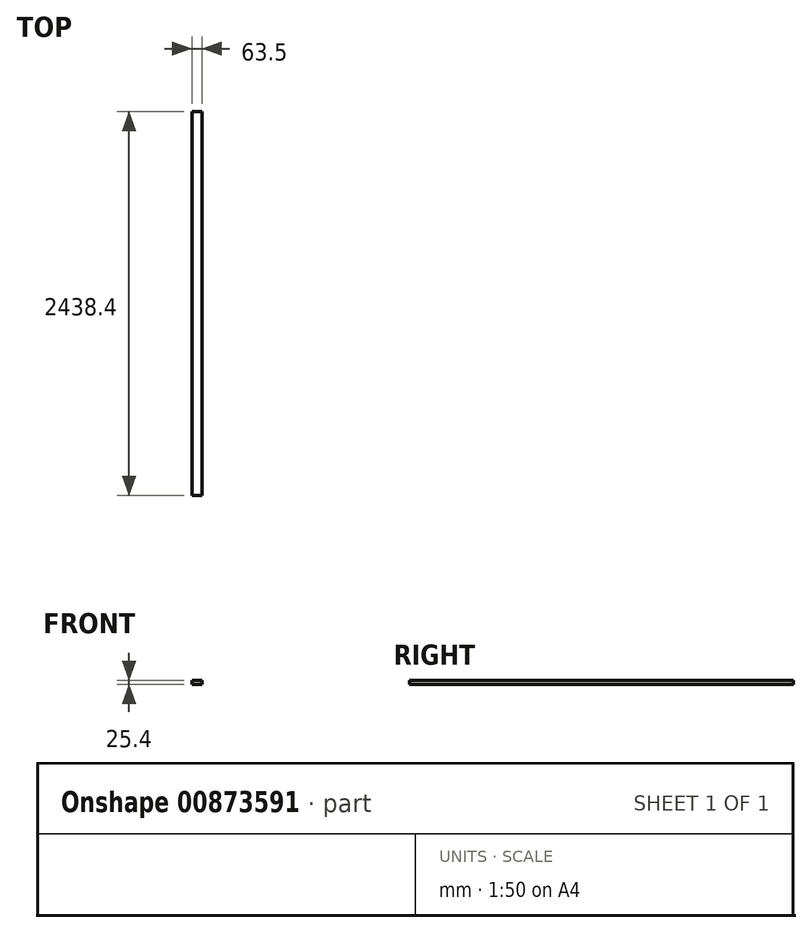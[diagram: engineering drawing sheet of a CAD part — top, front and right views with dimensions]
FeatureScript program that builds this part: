
annotation { "Feature Type Name" : "Feature", "Feature Type Description" : "" }
export const myFeature = defineFeature(function(context is Context, id is Id, definition is map)
    precondition{}
    {
        {
            var Q0;
            Q0=qCreatedBy(makeId("Top.planeOp"),FACE);
            var sketch = newSketch(context, id + "F0", { "sketchPlane" : qUnion([Q0])});
            skLineSegment(sketch, "E0.bottom", {"start": v(0, 0) * mm, "end": v(63.5, 0) * mm});
            skLineSegment(sketch, "E0.top", {"start": v(0, 2438.4) * mm, "end": v(63.5, 2438.4) * mm});
            skLineSegment(sketch, "E0.left", {"start": v(0, 0) * mm, "end": v(0, 2438.4) * mm});
            skLineSegment(sketch, "E0.right", {"start": v(63.5, 0) * mm, "end": v(63.5, 2438.4) * mm});
            skSolve(sketch);
        }
        {
            var Q0;
            Q0=qSketchRegion(id+"F0",true);
            extrude(context, id + "F1", {"entities" : qUnion([Q0]), "depth" : 25.4 * mm, "offsetDistance" : 25.4 * mm});
        }
    });
